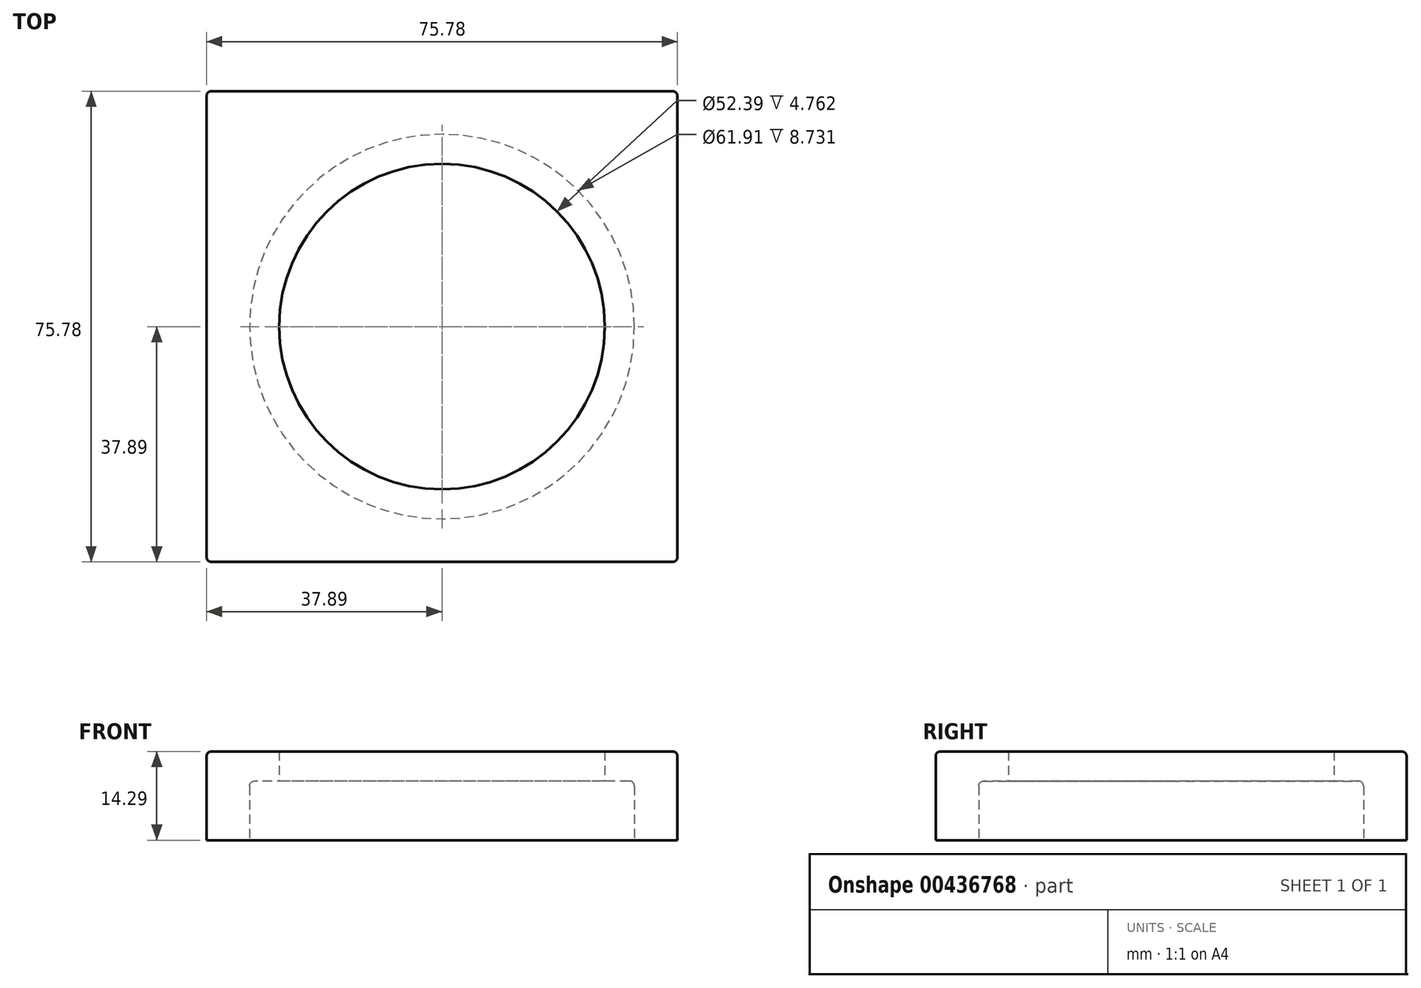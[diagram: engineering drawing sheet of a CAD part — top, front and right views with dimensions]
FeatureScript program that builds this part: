
annotation { "Feature Type Name" : "Feature", "Feature Type Description" : "" }
export const myFeature = defineFeature(function(context is Context, id is Id, definition is map)
    precondition{}
    {
        {
            var Q0;
            Q0=qCreatedBy(makeId("Top.planeOp"),FACE);
            var sketch = newSketch(context, id + "F0", { "sketchPlane" : qUnion([Q0])});
            skLineSegment(sketch, "E0.0", {"start": v(37.89, 37.89) * mm, "end": v(37.89, -37.89) * mm});
            skLineSegment(sketch, "E0.1", {"start": v(37.89, -37.89) * mm, "end": v(-37.89, -37.89) * mm});
            skLineSegment(sketch, "E0.2", {"start": v(-37.89, -37.89) * mm, "end": v(-37.89, 37.89) * mm});
            skLineSegment(sketch, "E0.3", {"start": v(-37.89, 37.89) * mm, "end": v(37.89, 37.89) * mm});
            skPoint(sketch, "E0.0.midPoint", {"position": v(37.89, 0) * mm});
            skCircle(sketch, "E1", {"center": v(0, 0) * mm, "radius": 26.2 * mm});
            skSolve(sketch);
        }
        {
            var Q0;
            Q0=makeQuery(id+"F0.imprint","IMPRINT",FACE,{"disambiguationData":[TD([[makeQuery(id+"F0.imprint","IMPRINT",EDGE,{"derivedFrom":sQuery(id+"F0.wireOp",EDGE,"E0.0")}),-1.0]])]});
            extrude(context, id + "F1", {"entities" : qUnion([Q0]), "depth" : 14.29 * mm});
        }
        {
            var Q0;
            Q0=qCreatedBy(makeId("Top.planeOp"),FACE);
            var sketch = newSketch(context, id + "F2", { "sketchPlane" : qUnion([Q0])});
            skCircle(sketch, "E2", {"center": v(0, 0) * mm, "radius": 30.96 * mm});
            skSolve(sketch);
        }
        {
            var Q0;
            Q0=makeQuery(id+"F2.imprint","IMPRINT",FACE,{"disambiguationData":[TD([[makeQuery(id+"F2.imprint","IMPRINT",EDGE,{"derivedFrom":sQuery(id+"F2.wireOp",EDGE,"E2")}),1.0]])]});
            extrude(context, id + "F3", {"entities" : qUnion([Q0]), "operationType" : NewBodyOperationType.REMOVE, "depth" : 9.52 * mm});
        }
        {
            var Q0;
            Q0=makeQuery(id+"F3.boolean.opBoolean","COPY",EDGE,{"derivedFrom":makeQuery(id+"F3.opExtrude","CAP_EDGE",EDGE,{"disambiguationData":[OSD([sQuery(id+"F2.wireOp",EDGE,"E2")])],"isStart":false})});
            var Q1;
            Q1=makeQuery(id+"F1.opExtrude","SWEPT_EDGE",EDGE,{"disambiguationData":[OSD([sQuery(id+"F0.wireOp",EDGE,"E0.1"),sQuery(id+"F0.wireOp",EDGE,"E0.2")])]});
            var Q2;
            Q2=makeQuery(id+"F1.opExtrude","SWEPT_EDGE",EDGE,{"disambiguationData":[OSD([sQuery(id+"F0.wireOp",EDGE,"E0.0"),sQuery(id+"F0.wireOp",EDGE,"E0.1")])]});
            var Q3;
            Q3=makeQuery(id+"F1.opExtrude","SWEPT_EDGE",EDGE,{"disambiguationData":[OSD([sQuery(id+"F0.wireOp",EDGE,"E0.0"),sQuery(id+"F0.wireOp",EDGE,"E0.3")])]});
            var Q4;
            Q4=makeQuery(id+"F1.opExtrude","SWEPT_EDGE",EDGE,{"disambiguationData":[OSD([sQuery(id+"F0.wireOp",EDGE,"E0.2"),sQuery(id+"F0.wireOp",EDGE,"E0.3")])]});
            var Q5;
            Q5=makeQuery(id+"F1.opExtrude","CAP_EDGE",EDGE,{"disambiguationData":[OSD([sQuery(id+"F0.wireOp",EDGE,"E0.1")])],"isStart":false});
            var Q6;
            Q6=makeQuery(id+"F1.opExtrude","CAP_EDGE",EDGE,{"disambiguationData":[OSD([sQuery(id+"F0.wireOp",EDGE,"E0.2")])],"isStart":false});
            var Q7;
            Q7=makeQuery(id+"F1.opExtrude","CAP_EDGE",EDGE,{"disambiguationData":[OSD([sQuery(id+"F0.wireOp",EDGE,"E0.3")])],"isStart":false});
            var Q8;
            Q8=makeQuery(id+"F1.opExtrude","CAP_EDGE",EDGE,{"disambiguationData":[OSD([sQuery(id+"F0.wireOp",EDGE,"E0.0")])],"isStart":false});
            fillet(context, id + "F4", {"entities" : qUnion([Q0, Q1, Q2, Q3, Q4, Q5, Q6, Q7, Q8]), "radius" : 0.8 * mm, "tangentPropagation" : true, "allowEdgeOverflow" : false});
        }
    });
